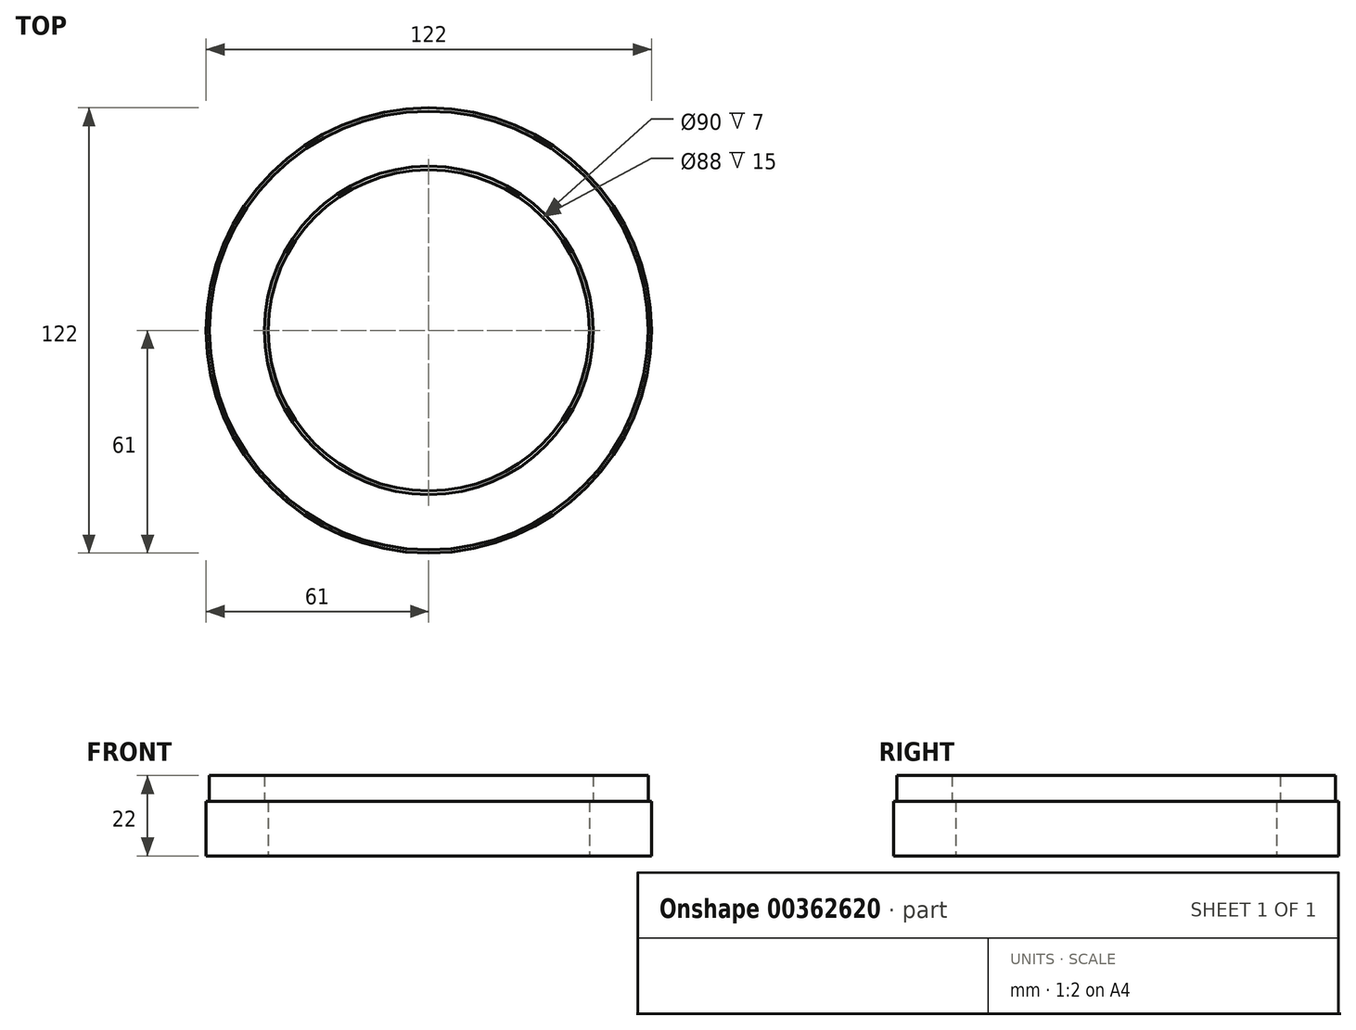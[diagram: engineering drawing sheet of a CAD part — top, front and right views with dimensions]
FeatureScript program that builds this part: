
annotation { "Feature Type Name" : "Feature", "Feature Type Description" : "" }
export const myFeature = defineFeature(function(context is Context, id is Id, definition is map)
    precondition{}
    {
        {
            var Q0;
            Q0=qCreatedBy(makeId("Top.planeOp"),FACE);
            var sketch = newSketch(context, id + "F0", { "sketchPlane" : qUnion([Q0])});
            skCircle(sketch, "E0", {"center": v(0, 0) * mm, "radius": 45 * mm});
            skCircle(sketch, "E1", {"center": v(0, 0) * mm, "radius": 60.1 * mm});
            skCircle(sketch, "E2", {"center": v(0, 0) * mm, "radius": 61 * mm});
            skCircle(sketch, "E3", {"center": v(0, 0) * mm, "radius": 44 * mm});
            skSolve(sketch);
        }
        {
            var Q0;
            Q0=makeQuery(id+"F0.imprint","IMPRINT",FACE,{"disambiguationData":[TD([[makeQuery(id+"F0.imprint","IMPRINT",EDGE,{"derivedFrom":sQuery(id+"F0.wireOp",EDGE,"E0")}),-1.0]])]});
            extrude(context, id + "F1", {"entities" : qUnion([Q0]), "depth" : 22 * mm, "offsetDistance" : 25 * mm});
        }
        {
            var Q0;
            Q0 = qSketchRegion(id + "F0", true);
            extrude(context, id + "F2", {"entities" : qUnion([Q0]), "operationType" : NewBodyOperationType.ADD, "depth" : 15 * mm, "offsetDistance" : 25 * mm});
        }
        {
            var Q0;
            Q0=makeQuery(id+"F0.imprint","IMPRINT",FACE,{"disambiguationData":[TD([[makeQuery(id+"F0.imprint","IMPRINT",EDGE,{"derivedFrom":sQuery(id+"F0.wireOp",EDGE,"E0")}),1.0]])]});
            extrude(context, id + "F3", {"entities" : qUnion([Q0]), "operationType" : NewBodyOperationType.ADD, "depth" : 15 * mm, "offsetDistance" : 25 * mm});
        }
    });
